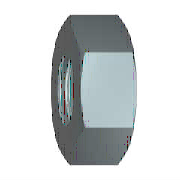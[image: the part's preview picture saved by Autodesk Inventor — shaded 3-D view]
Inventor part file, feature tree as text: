
AUTODESK INVENTOR PART (.ipt)
format: ipt  version: 2015 (Build 190159000, 159)  size: 171,008 bytes
history: native  units: mm (DEFAULTED — no unit token found)
features: sketch x3, chamfer x1, hole x1, other x1, plane x1
ambient origin geometry x7: Origin, YZ Plane, XZ Plane, X Axis, Y Axis, Z Axis, Center Point
bodies: Solid1 (feature_tree), Body (feature_tree)
feature tree (7):
  chamfer  "Chamfer1"  Angle=30.0deg  [1 undecoded]
  hole  "Thread"  [1 undecoded]
  other  "Work Axis1"
  plane  "Work Plane1"
  sketch  "Sketch1"  dims[d0=12.83161mm]
  sketch  "Sketch2"  dims[d1=5.5626mm]
  sketch  "Sketch3"  dims[d2=0.0mm d3=30.0deg d4=30.0deg d5=11.1125mm d6=11.1125mm d7=90.0deg d25=4.9784mm d26=6.0mm d27=4.0mm d28=2.0mm d29=14.3117mm d30=8.0mm d31=20.594885mm d8=0.687408mm d9=30.0deg d10=0.687408mm d11=30.0deg d13=0.0mm d14=0.0mm d39=0.0mm d40=0.687408mm d41=0.687408mm d42=0.0mm]
note: 2 required parameter values undecoded (feature->parameter linkage not recoverable at this tier; creation-order binding heuristic only, values carry confidence <= 0.55)
